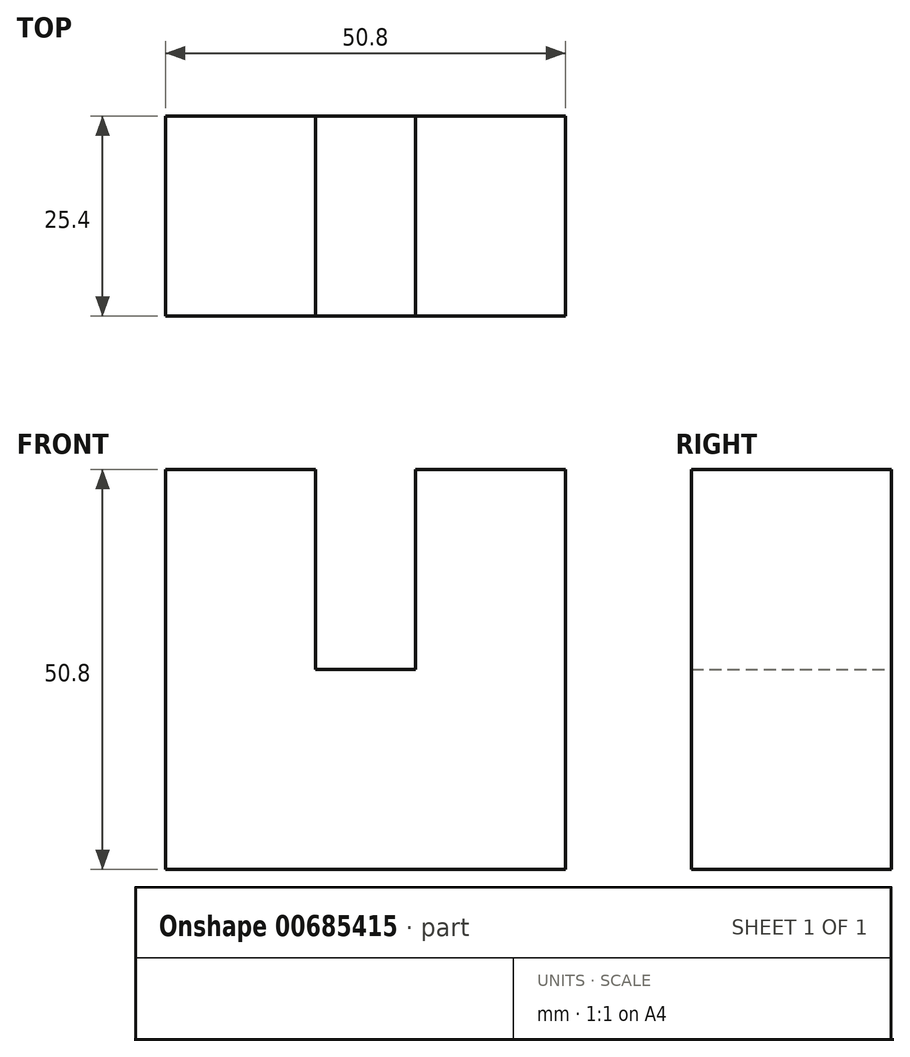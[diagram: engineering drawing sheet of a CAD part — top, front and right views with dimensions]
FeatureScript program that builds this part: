
annotation { "Feature Type Name" : "Feature", "Feature Type Description" : "" }
export const myFeature = defineFeature(function(context is Context, id is Id, definition is map)
    precondition{}
    {
        {
            var Q0;
            Q0=qCreatedBy(makeId("Front.planeOp"),FACE);
            var sketch = newSketch(context, id + "F0", { "sketchPlane" : qUnion([Q0])});
            skLineSegment(sketch, "E0", {"start": v(0, 0) * mm, "end": v(0, 50.8) * mm});
            skLineSegment(sketch, "E1", {"start": v(0, 50.8) * mm, "end": v(19.05, 50.8) * mm});
            skLineSegment(sketch, "E2", {"start": v(19.05, 50.8) * mm, "end": v(19.05, 25.4) * mm});
            skLineSegment(sketch, "E3", {"start": v(19.05, 25.4) * mm, "end": v(31.75, 25.4) * mm});
            skLineSegment(sketch, "E4", {"start": v(31.75, 25.4) * mm, "end": v(31.75, 50.8) * mm});
            skLineSegment(sketch, "E5", {"start": v(31.75, 50.8) * mm, "end": v(50.8, 50.8) * mm});
            skLineSegment(sketch, "E6", {"start": v(50.8, 50.8) * mm, "end": v(50.8, 0) * mm});
            skLineSegment(sketch, "E7", {"start": v(50.8, 0) * mm, "end": v(0, 0) * mm});
            skSolve(sketch);
        }
        {
            var Q0;
            Q0=makeQuery(id+"F0.imprint","IMPRINT",FACE,{"disambiguationData":[TD([[makeQuery(id+"F0.imprint","IMPRINT",EDGE,{"derivedFrom":sQuery(id+"F0.wireOp",EDGE,"E0")}),-1.0]])]});
            extrude(context, id + "F1", {"entities" : qUnion([Q0]), "depth" : 25.4 * mm, "offsetDistance" : 25.4 * mm});
        }
    });
